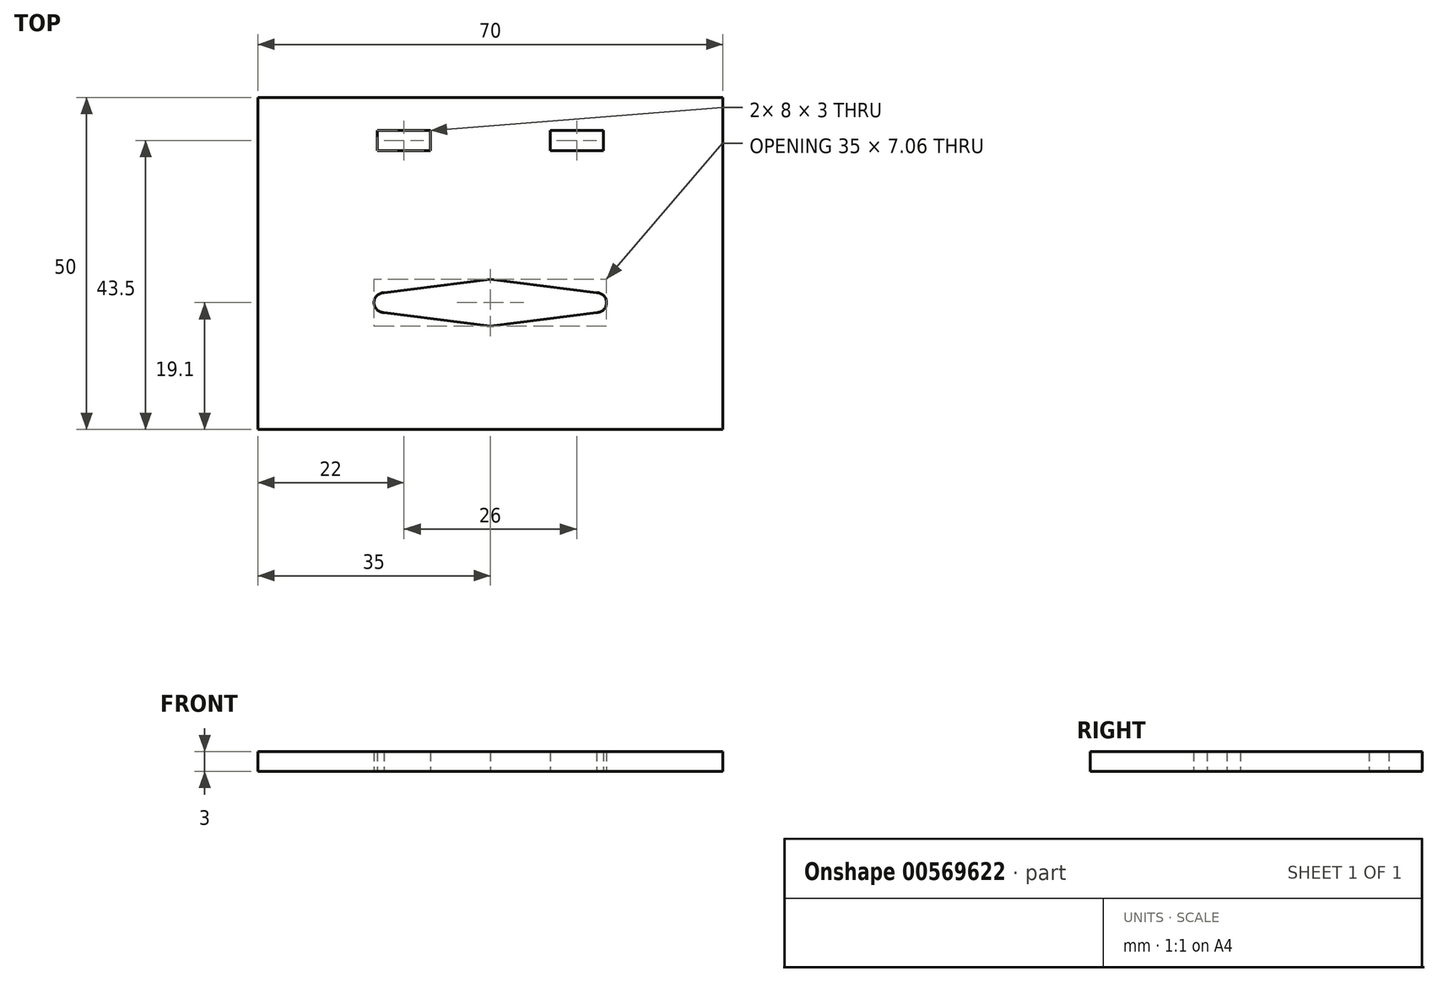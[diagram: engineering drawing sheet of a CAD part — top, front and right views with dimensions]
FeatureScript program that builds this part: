
annotation { "Feature Type Name" : "Feature", "Feature Type Description" : "" }
export const myFeature = defineFeature(function(context is Context, id is Id, definition is map)
    precondition{}
    {
        {
            var Q0;
            Q0=qCreatedBy(makeId("Top.planeOp"),FACE);
            var sketch = newSketch(context, id + "F0", { "sketchPlane" : qUnion([Q0])});
            skLineSegment(sketch, "E0.bottom", {"start": v(-35, 30.9) * mm, "end": v(35, 30.9) * mm});
            skLineSegment(sketch, "E0.top", {"start": v(-35, -19.1) * mm, "end": v(35, -19.1) * mm});
            skLineSegment(sketch, "E0.left", {"start": v(-35, 30.9) * mm, "end": v(-35, -19.1) * mm});
            skLineSegment(sketch, "E0.right", {"start": v(35, 30.9) * mm, "end": v(35, -19.1) * mm});
            skLineSegment(sketch, "E1", {"start": v(-56.05, 25.9) * mm, "end": v(44.58, 25.9) * mm, "construction": true});
            skLineSegment(sketch, "E2", {"start": v(-56.93, 22.9) * mm, "end": v(45.17, 22.9) * mm, "construction": true});
            skLineSegment(sketch, "E3.bottom", {"start": v(-17, 25.9) * mm, "end": v(-9, 25.9) * mm});
            skLineSegment(sketch, "E3.top", {"start": v(-17, 22.9) * mm, "end": v(-9, 22.9) * mm});
            skLineSegment(sketch, "E3.left", {"start": v(-17, 25.9) * mm, "end": v(-17, 22.9) * mm});
            skLineSegment(sketch, "E3.right", {"start": v(-9, 25.9) * mm, "end": v(-9, 22.9) * mm});
            skLineSegment(sketch, "E4.bottom", {"start": v(9, 25.9) * mm, "end": v(17, 25.9) * mm});
            skLineSegment(sketch, "E4.top", {"start": v(9, 22.9) * mm, "end": v(17, 22.9) * mm});
            skLineSegment(sketch, "E4.left", {"start": v(9, 25.9) * mm, "end": v(9, 22.9) * mm});
            skLineSegment(sketch, "E4.right", {"start": v(17, 25.9) * mm, "end": v(17, 22.9) * mm});
            skCircle(sketch, "E5", {"center": v(0, 0) * mm, "radius": 3.5 * mm});
            skArc(sketch, "E6", {"start": v(-16, 1.5) * mm, "mid": v(-17.5, 0) * mm, "end": v(-16, -1.5) * mm});
            skArc(sketch, "E7", {"start": v(16, -1.5) * mm, "mid": v(17.5, 0) * mm, "end": v(16, 1.5) * mm});
            skLineSegment(sketch, "E8", {"start": v(-16, 1.5) * mm, "end": v(0, 3.53) * mm});
            skLineSegment(sketch, "E9", {"start": v(0, 3.53) * mm, "end": v(16, 1.5) * mm});
            skLineSegment(sketch, "E10", {"start": v(16, -1.5) * mm, "end": v(0, -3.53) * mm});
            skPoint(sketch, "E11.end.orphan", {"position": v(-16, -1.51) * mm});
            skLineSegment(sketch, "E12", {"start": v(0, -3.53) * mm, "end": v(-16, -1.5) * mm});
            skSolve(sketch);
        }
        {
            var Q0;
            Q0=makeQuery(id+"F0.imprint","IMPRINT",FACE,{"disambiguationData":[TD([[makeQuery(id+"F0.imprint","IMPRINT",EDGE,{"derivedFrom":sQuery(id+"F0.wireOp",EDGE,"E0.bottom")}),-1.0]])]});
            extrude(context, id + "F1", {"entities" : qUnion([Q0]), "depth" : 3 * mm, "offsetDistance" : 25 * mm});
        }
    });
